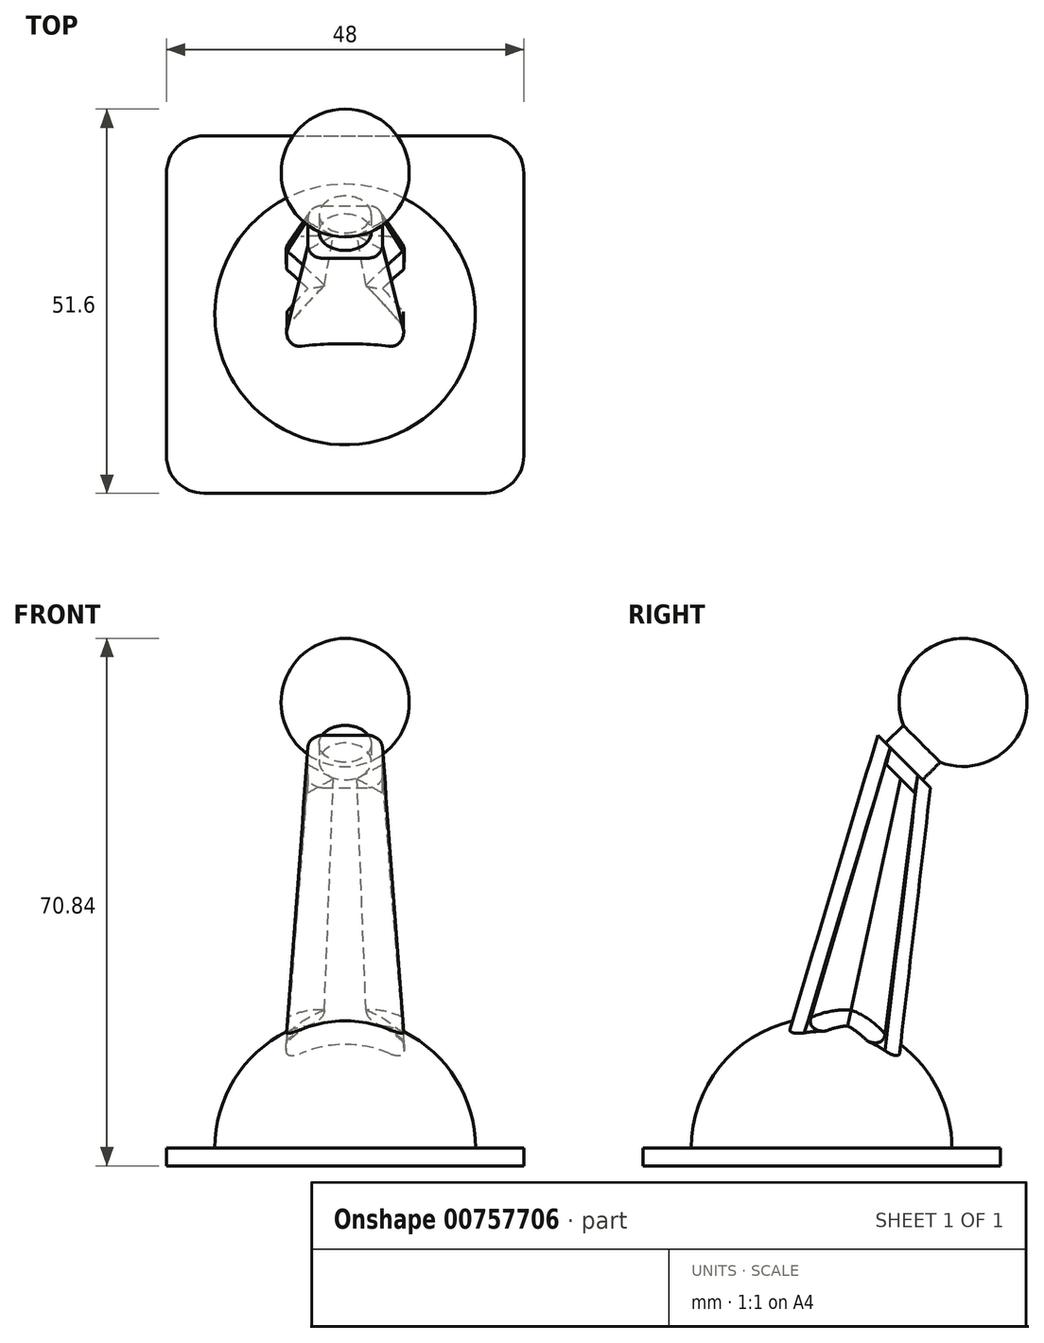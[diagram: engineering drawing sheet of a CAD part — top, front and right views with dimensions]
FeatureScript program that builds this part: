
annotation { "Feature Type Name" : "Feature", "Feature Type Description" : "" }
export const myFeature = defineFeature(function(context is Context, id is Id, definition is map)
    precondition{}
    {
        {
            var Q0;
            Q0=qCreatedBy(makeId("Top.planeOp"),FACE);
            var sketch = newSketch(context, id + "F0", { "sketchPlane" : qUnion([Q0])});
            skLineSegment(sketch, "E0.bottom", {"start": v(-24, 24) * mm, "end": v(24, 24) * mm});
            skLineSegment(sketch, "E0.top", {"start": v(-24, -24) * mm, "end": v(24, -24) * mm});
            skLineSegment(sketch, "E0.left", {"start": v(-24, 24) * mm, "end": v(-24, -24) * mm});
            skLineSegment(sketch, "E0.right", {"start": v(24, 24) * mm, "end": v(24, -24) * mm});
            skPoint(sketch, "E0.middle", {"position": v(0, 0) * mm});
            skSolve(sketch);
        }
        {
            var Q0;
            Q0 = qSketchRegion(id + "F0", true);
            extrude(context, id + "F1", {"entities" : qUnion([Q0]), "oppositeDirection" : true, "depth" : 2.4 * mm, "offsetDistance" : 25 * mm});
        }
        {
            var Q0;
            Q0=makeQuery(id+"F1.opExtrude","CAP_FACE",FACE,{"disambiguationData":[OSD([sQuery(id+"F0.wireOp",EDGE,"E0.bottom"),sQuery(id+"F0.wireOp",EDGE,"E0.top"),sQuery(id+"F0.wireOp",EDGE,"E0.left"),sQuery(id+"F0.wireOp",EDGE,"E0.right")])],"isStart":true});
            var sketch = newSketch(context, id + "F2", { "sketchPlane" : qUnion([Q0])});
            skLineSegment(sketch, "E1.bottom", {"start": v(-9, -9) * mm, "end": v(9, -9) * mm});
            skLineSegment(sketch, "E1.top", {"start": v(-9, 9) * mm, "end": v(9, 9) * mm});
            skLineSegment(sketch, "E1.left", {"start": v(-9, -9) * mm, "end": v(-9, 9) * mm});
            skLineSegment(sketch, "E1.right", {"start": v(9, -9) * mm, "end": v(9, 9) * mm});
            skPoint(sketch, "E1.middle", {"position": v(0, 0) * mm});
            skLineSegment(sketch, "E2", {"start": v(-9, 6.6) * mm, "end": v(-3.5, 0) * mm});
            skLineSegment(sketch, "E3", {"start": v(-3.5, 0) * mm, "end": v(-9, -6.6) * mm});
            skLineSegment(sketch, "E4", {"start": v(9, 6.6) * mm, "end": v(3.5, 0) * mm});
            skLineSegment(sketch, "E5", {"start": v(3.5, 0) * mm, "end": v(9, -6.6) * mm});
            skSolve(sketch);
        }
        {
            var Q0;
            {var subQ4=sQuery(id+"F2.wireOp",EDGE,"E1.bottom");Q0=makeQuery(id+"F2.imprint","IMPRINT",FACE,{"disambiguationData":[TD([[makeQuery(id+"F2.imprint","IMPRINT",EDGE,{"derivedFrom":subQ4}),-1.0]])]});}
            cPlane(context, id + "F3", {"entities" : qUnion([Q0]), "cplaneType" : CPlaneType.OFFSET, "offset" : 45 * mm, "width" : 150 * mm, "height" : 150 * mm});
        }
        {
            var Q0;
            Q0=qCreatedBy(id+"F3.planeOp",FACE);
            var sketch = newSketch(context, id + "F4", { "sketchPlane" : qUnion([Q0])});
            skLineSegment(sketch, "E6", {"start": v(11.73, 18) * mm, "end": v(-9.75, 18) * mm, "construction": true});
            skSolve(sketch);
        }
        {
            var Q0;
            Q0=sQuery(id+"F4.wireOp",EDGE,"E6");
            cPlane(context, id + "F5", {"entities" : qUnion([Q0]), "cplaneType" : CPlaneType.LINE_ANGLE, "offset" : 25 * mm, "angle" : 45 * degree, "oppositeDirection" : true, "width" : 150 * mm, "height" : 150 * mm});
        }
        {
            var Q0;
            Q0=qCreatedBy(id+"F5.planeOp",FACE);
            var sketch = newSketch(context, id + "F6", { "sketchPlane" : qUnion([Q0])});
            skLineSegment(sketch, "E7.bottom", {"start": v(-5, 23.87) * mm, "end": v(5, 23.87) * mm});
            skLineSegment(sketch, "E7.top", {"start": v(-5, 33.87) * mm, "end": v(5, 33.87) * mm});
            skLineSegment(sketch, "E7.left", {"start": v(-5, 23.87) * mm, "end": v(-5, 33.87) * mm});
            skLineSegment(sketch, "E7.right", {"start": v(5, 23.87) * mm, "end": v(5, 33.87) * mm});
            skPoint(sketch, "E7.middle", {"position": v(0, 28.87) * mm});
            skLineSegment(sketch, "E8", {"start": v(5, 31.47) * mm, "end": v(1.5, 28.87) * mm});
            skLineSegment(sketch, "E9", {"start": v(1.5, 28.87) * mm, "end": v(5, 26.27) * mm});
            skLineSegment(sketch, "E10", {"start": v(-5, 31.47) * mm, "end": v(-1.5, 28.87) * mm});
            skLineSegment(sketch, "E11", {"start": v(-1.5, 28.87) * mm, "end": v(-5, 26.35) * mm});
            skSolve(sketch);
        }
        {
            var Q1;
            {var subQ3=sQuery(id+"F2.wireOp",EDGE,"E1.bottom");Q1=makeQuery(id+"F2.imprint","IMPRINT",FACE,{"disambiguationData":[TD([[makeQuery(id+"F2.imprint","IMPRINT",EDGE,{"derivedFrom":subQ3}),1.0]])]});}
            var Q2;
            {var subQ3=sQuery(id+"F6.wireOp",EDGE,"E7.bottom");Q2=makeQuery(id+"F6.imprint","IMPRINT",FACE,{"disambiguationData":[TD([[makeQuery(id+"F6.imprint","IMPRINT",EDGE,{"derivedFrom":subQ3}),1.0]])]});}
            loft(context, id + "F7", {"operationType" : NewBodyOperationType.ADD, "sheetProfilesArray" : [{ "sheetProfileEntities" : qUnion([Q1]) }, { "sheetProfileEntities" : qUnion([Q2]) }]});
        }
        {
            var Q0;
            {var subQ0=sQuery(id+"F6.wireOp",EDGE,"E8");Q0=makeQuery(id+"F6.imprint","IMPRINT",FACE,{"disambiguationData":[TD([[makeQuery(id+"F6.imprint","IMPRINT",EDGE,{"derivedFrom":subQ0}),1.0]])]});}
            var Q1;
            {var subQ3=sQuery(id+"F6.wireOp",EDGE,"E7.bottom");Q1=makeQuery(id+"F6.imprint","IMPRINT",FACE,{"disambiguationData":[TD([[makeQuery(id+"F6.imprint","IMPRINT",EDGE,{"derivedFrom":subQ3}),1.0]])]});}
            var Q2;
            {var subQ0=sQuery(id+"F6.wireOp",EDGE,"E10");Q2=makeQuery(id+"F6.imprint","IMPRINT",FACE,{"disambiguationData":[TD([[makeQuery(id+"F6.imprint","IMPRINT",EDGE,{"derivedFrom":subQ0}),-1.0]])]});}
            extrude(context, id + "F8", {"entities" : qUnion([Q0, Q1, Q2]), "operationType" : NewBodyOperationType.ADD, "depth" : 2 * mm, "offsetDistance" : 25 * mm});
        }
        {
            var Q0;
            {var subQ3=sQuery(id+"F6.wireOp",EDGE,"E7.bottom");Q0=makeQuery(id+"F6.imprint","IMPRINT",FACE,{"disambiguationData":[TD([[makeQuery(id+"F6.imprint","IMPRINT",EDGE,{"derivedFrom":subQ3}),1.0]])]});}
            var sketch = newSketch(context, id + "F9", { "sketchPlane" : qUnion([Q0])});
            skCircle(sketch, "E12", {"center": v(0, 28.87) * mm, "radius": 3.5 * mm});
            skSolve(sketch);
        }
        {
            var Q0;
            Q0=makeQuery(id+"F9.imprint","IMPRINT",FACE,{"disambiguationData":[TD([[makeQuery(id+"F9.imprint","IMPRINT",EDGE,{"derivedFrom":sQuery(id+"F9.wireOp",EDGE,"E12")}),1.0]])]});
            var Q1;
            {var subQ0=sQuery(id+"F9.wireOp",EDGE,"E12");var subQ1=makeQuery(id+"F6.imprint","IMPRINT",EDGE,{"derivedFrom":sQuery(id+"F6.wireOp",EDGE,"E10")});var subQ2=makeQuery(id+"F9.imprint","INTERSECT",VERTEX,{"derivedFrom":[subQ1,subQ0]});Q1=makeQuery(id+"F9.imprint","IMPRINT",FACE,{"disambiguationData":[TD([[makeQuery(id+"F9.imprint","IMPRINT",EDGE,{"disambiguationData":[TD([[subQ2,-1.0]])],"derivedFrom":subQ0}),1.0]])]});}
            var Q2;
            {var subQ0=sQuery(id+"F9.wireOp",EDGE,"E12");var subQ1=makeQuery(id+"F6.imprint","IMPRINT",EDGE,{"derivedFrom":sQuery(id+"F6.wireOp",EDGE,"E8")});var subQ2=makeQuery(id+"F9.imprint","INTERSECT",VERTEX,{"derivedFrom":[subQ1,subQ0]});Q2=makeQuery(id+"F9.imprint","IMPRINT",FACE,{"disambiguationData":[TD([[makeQuery(id+"F9.imprint","IMPRINT",EDGE,{"disambiguationData":[TD([[subQ2,1.0]])],"derivedFrom":subQ0}),1.0]])]});}
            extrude(context, id + "F10", {"entities" : qUnion([Q0, Q1, Q2]), "operationType" : NewBodyOperationType.ADD, "oppositeDirection" : true, "depth" : 3.4 * mm, "offsetDistance" : 25 * mm});
        }
        {
            var Q0;
            Q0=qCreatedBy(makeId("Right.planeOp"),FACE);
            var sketch = newSketch(context, id + "F11", { "sketchPlane" : qUnion([Q0])});
            skLineSegment(sketch, "E13", {"start": v(11.06, 51.9) * mm, "end": v(-10.15, 30.68) * mm, "construction": true});
            skArc(sketch, "E14", {"start": v(12.92, 53.76) * mm, "mid": v(25.08, 53.76) * mm, "end": v(25.08, 65.92) * mm});
            skLineSegment(sketch, "E15", {"start": v(8.17, 59.63) * mm, "end": v(21.18, 46.63) * mm, "construction": true});
            skLineSegment(sketch, "E16", {"start": v(11.82, 47.7) * mm, "end": v(6.68, 42.56) * mm, "construction": true});
            skLineSegment(sketch, "E17", {"start": v(12.92, 53.76) * mm, "end": v(25.08, 65.92) * mm});
            skSolve(sketch);
        }
        {
            var Q0;
            Q0=makeQuery(id+"F11.imprint","IMPRINT",FACE,{"disambiguationData":[TD([[makeQuery(id+"F11.imprint","IMPRINT",EDGE,{"derivedFrom":sQuery(id+"F11.wireOp",EDGE,"E14")}),1.0]])]});
            var Q1;
            Q1=sQuery(id+"F11.wireOp",EDGE,"E13");
            revolve(context, id + "F12", {"operationType" : NewBodyOperationType.ADD, "surfaceOperationType" : NewSurfaceOperationType.NEW, "entities" : qUnion([Q0]), "axis" : qUnion([Q1]), "revolveType" : RevolveType.FULL});
        }
        {
            var Q0;
            Q0=qCreatedBy(makeId("Right.planeOp"),FACE);
            var sketch = newSketch(context, id + "F13", { "sketchPlane" : qUnion([Q0])});
            skArc(sketch, "E18", {"start": v(0, 17.5) * mm, "mid": v(-12.37, 12.37) * mm, "end": v(-17.5, 0) * mm});
            skLineSegment(sketch, "E19", {"start": v(-17.5, 0) * mm, "end": v(0, 0) * mm});
            skLineSegment(sketch, "E20", {"start": v(0, 0) * mm, "end": v(0, 27.64) * mm, "construction": true});
            skPoint(sketch, "E20.endSnap0", {"position": v(0, 17.5) * mm});
            skLineSegment(sketch, "E21", {"start": v(0, 17.5) * mm, "end": v(0, 0) * mm});
            skSolve(sketch);
        }
        {
            var Q0;
            Q0 = qSketchRegion(id + "F13", true);
            var Q1;
            Q1=sQuery(id+"F13.wireOp",EDGE,"E20");
            revolve(context, id + "F14", {"operationType" : NewBodyOperationType.ADD, "surfaceOperationType" : NewSurfaceOperationType.NEW, "entities" : qUnion([Q0]), "axis" : qUnion([Q1]), "revolveType" : RevolveType.FULL});
        }
        {
            var Q0;
            {var subQ1=sQuery(id+"F6.wireOp",EDGE,"E7.left");var subQ2=sQuery(id+"F6.wireOp",EDGE,"E7.top");Q0=makeQuery(id+"F8.boolean.opBoolean","SPLIT",FACE,{"disambiguationData":[TD([makeQuery(id+"F8.opExtrude","SWEPT_FACE",FACE,{"disambiguationData":[OSD([subQ2])]})])],"derivedFrom":makeQuery(id+"F8.opExtrude","SWEPT_FACE",FACE,{"disambiguationData":[OSD([subQ1])]})});}
            extrude(context, id + "F15", {"entities" : qUnion([Q0]), "operationType" : NewBodyOperationType.REMOVE, "oppositeDirection" : true, "depth" : 25 * mm, "offsetDistance" : 25 * mm});
        }
        {
            var Q0;
            Q0=makeQuery(id+"F7.opLoft","SWEPT_EDGE",EDGE,{"disambiguationData":[OSD([sQuery(id+"F2.wireOp",EDGE,"E1.top"),sQuery(id+"F2.wireOp",EDGE,"E1.left"),sQuery(id+"F6.wireOp",EDGE,"E7.bottom"),sQuery(id+"F6.wireOp",EDGE,"E7.left")])]});
            var Q1;
            Q1=makeQuery(id+"F7.opLoft","SWEPT_EDGE",EDGE,{"disambiguationData":[OSD([sQuery(id+"F2.wireOp",EDGE,"E1.bottom"),sQuery(id+"F2.wireOp",EDGE,"E1.left"),sQuery(id+"F6.wireOp",EDGE,"E7.top"),sQuery(id+"F6.wireOp",EDGE,"E7.left")])]});
            var Q2;
            Q2=makeQuery(id+"F7.opLoft","SWEPT_EDGE",EDGE,{"disambiguationData":[OSD([sQuery(id+"F2.wireOp",EDGE,"E1.bottom"),sQuery(id+"F2.wireOp",EDGE,"E1.right"),sQuery(id+"F6.wireOp",EDGE,"E7.top"),sQuery(id+"F6.wireOp",EDGE,"E7.right")])]});
            var Q3;
            Q3=makeQuery(id+"F7.opLoft","SWEPT_EDGE",EDGE,{"disambiguationData":[OSD([sQuery(id+"F2.wireOp",EDGE,"E1.top"),sQuery(id+"F2.wireOp",EDGE,"E1.right"),sQuery(id+"F6.wireOp",EDGE,"E7.bottom"),sQuery(id+"F6.wireOp",EDGE,"E7.right")])]});
            var Q4;
            {var subQ0=sQuery(id+"F6.wireOp",EDGE,"E10");var subQ1=sQuery(id+"F6.wireOp",EDGE,"E11");var subQ2=sQuery(id+"F6.wireOp",EDGE,"E7.left");var subQ3=sQuery(id+"F2.wireOp",EDGE,"E3");var subQ4=sQuery(id+"F2.wireOp",EDGE,"E1.left");var subQ5=sQuery(id+"F2.wireOp",EDGE,"E2");Q4=makeQuery(id+"F14.boolean.opBoolean","INTERSECT",EDGE,{"derivedFrom":[makeQuery(id+"F7.opLoft","SWEPT_FACE",FACE,{"disambiguationData":[OSD([subQ4,subQ5,subQ3,subQ2,subQ0,subQ1]),TDD([makeQuery(id+"F2.imprint","INTERSECT",VERTEX,{"derivedFrom":[subQ5,subQ3]}),makeQuery(id+"F2.imprint","INTERSECT",VERTEX,{"derivedFrom":[subQ4,subQ3]}),makeQuery(id+"F2.imprint","IMPRINT",EDGE,{"derivedFrom":subQ3}),makeQuery(id+"F6.imprint","INTERSECT",VERTEX,{"derivedFrom":[subQ2,subQ0]}),makeQuery(id+"F6.imprint","INTERSECT",VERTEX,{"derivedFrom":[subQ0,subQ1]}),makeQuery(id+"F6.imprint","IMPRINT",EDGE,{"derivedFrom":subQ0})])]}),makeQuery(id+"F14.opRevolve","SWEPT_FACE",FACE,{"disambiguationData":[OSD([sQuery(id+"F13.wireOp",EDGE,"E18")])]})]});}
            var Q5;
            {var subQ0=sQuery(id+"F6.wireOp",EDGE,"E11");var subQ1=sQuery(id+"F6.wireOp",EDGE,"E7.left");var subQ2=sQuery(id+"F6.wireOp",EDGE,"E10");var subQ3=sQuery(id+"F2.wireOp",EDGE,"E2");var subQ4=sQuery(id+"F2.wireOp",EDGE,"E3");var subQ5=sQuery(id+"F2.wireOp",EDGE,"E1.left");Q5=makeQuery(id+"F14.boolean.opBoolean","INTERSECT",EDGE,{"derivedFrom":[makeQuery(id+"F7.opLoft","SWEPT_FACE",FACE,{"disambiguationData":[OSD([subQ5,subQ3,subQ4,subQ1,subQ2,subQ0]),TDD([makeQuery(id+"F2.imprint","INTERSECT",VERTEX,{"derivedFrom":[subQ5,subQ3]}),makeQuery(id+"F2.imprint","INTERSECT",VERTEX,{"derivedFrom":[subQ3,subQ4]}),makeQuery(id+"F2.imprint","IMPRINT",EDGE,{"derivedFrom":subQ3}),makeQuery(id+"F6.imprint","INTERSECT",VERTEX,{"derivedFrom":[subQ2,subQ0]}),makeQuery(id+"F6.imprint","INTERSECT",VERTEX,{"derivedFrom":[subQ1,subQ0]}),makeQuery(id+"F6.imprint","IMPRINT",EDGE,{"derivedFrom":subQ0})])]}),makeQuery(id+"F14.opRevolve","SWEPT_FACE",FACE,{"disambiguationData":[OSD([sQuery(id+"F13.wireOp",EDGE,"E18")])]})]});}
            var Q6;
            {var subQ0=sQuery(id+"F6.wireOp",EDGE,"E8");var subQ1=sQuery(id+"F6.wireOp",EDGE,"E9");var subQ2=sQuery(id+"F6.wireOp",EDGE,"E7.right");var subQ3=sQuery(id+"F2.wireOp",EDGE,"E5");var subQ4=sQuery(id+"F2.wireOp",EDGE,"E1.right");var subQ5=sQuery(id+"F2.wireOp",EDGE,"E4");Q6=makeQuery(id+"F14.boolean.opBoolean","INTERSECT",EDGE,{"derivedFrom":[makeQuery(id+"F7.opLoft","SWEPT_FACE",FACE,{"disambiguationData":[OSD([subQ4,subQ5,subQ3,subQ2,subQ0,subQ1]),TDD([makeQuery(id+"F2.imprint","INTERSECT",VERTEX,{"derivedFrom":[subQ5,subQ3]}),makeQuery(id+"F2.imprint","INTERSECT",VERTEX,{"derivedFrom":[subQ4,subQ3]}),makeQuery(id+"F2.imprint","IMPRINT",EDGE,{"derivedFrom":subQ3}),makeQuery(id+"F6.imprint","INTERSECT",VERTEX,{"derivedFrom":[subQ2,subQ0]}),makeQuery(id+"F6.imprint","INTERSECT",VERTEX,{"derivedFrom":[subQ0,subQ1]}),makeQuery(id+"F6.imprint","IMPRINT",EDGE,{"derivedFrom":subQ0})])]}),makeQuery(id+"F14.opRevolve","SWEPT_FACE",FACE,{"disambiguationData":[OSD([sQuery(id+"F13.wireOp",EDGE,"E18")])]})]});}
            var Q7;
            {var subQ0=sQuery(id+"F6.wireOp",EDGE,"E9");var subQ1=sQuery(id+"F6.wireOp",EDGE,"E7.right");var subQ2=sQuery(id+"F6.wireOp",EDGE,"E8");var subQ3=sQuery(id+"F2.wireOp",EDGE,"E4");var subQ4=sQuery(id+"F2.wireOp",EDGE,"E5");var subQ5=sQuery(id+"F2.wireOp",EDGE,"E1.right");Q7=makeQuery(id+"F14.boolean.opBoolean","INTERSECT",EDGE,{"derivedFrom":[makeQuery(id+"F7.opLoft","SWEPT_FACE",FACE,{"disambiguationData":[OSD([subQ5,subQ3,subQ4,subQ1,subQ2,subQ0]),TDD([makeQuery(id+"F2.imprint","INTERSECT",VERTEX,{"derivedFrom":[subQ5,subQ3]}),makeQuery(id+"F2.imprint","INTERSECT",VERTEX,{"derivedFrom":[subQ3,subQ4]}),makeQuery(id+"F2.imprint","IMPRINT",EDGE,{"derivedFrom":subQ3}),makeQuery(id+"F6.imprint","INTERSECT",VERTEX,{"derivedFrom":[subQ2,subQ0]}),makeQuery(id+"F6.imprint","INTERSECT",VERTEX,{"derivedFrom":[subQ1,subQ0]}),makeQuery(id+"F6.imprint","IMPRINT",EDGE,{"derivedFrom":subQ0})])]}),makeQuery(id+"F14.opRevolve","SWEPT_FACE",FACE,{"disambiguationData":[OSD([sQuery(id+"F13.wireOp",EDGE,"E18")])]})]});}
            fillet(context, id + "F16", {"entities" : qUnion([Q0, Q1, Q2, Q3, Q4, Q5, Q6, Q7]), "radius" : 2 * mm, "tangentPropagation" : true, "allowEdgeOverflow" : false});
        }
        {
            var Q0;
            Q0=makeQuery(id+"F1.opExtrude","SWEPT_EDGE",EDGE,{"disambiguationData":[OSD([sQuery(id+"F0.wireOp",EDGE,"E0.bottom"),sQuery(id+"F0.wireOp",EDGE,"E0.right")])]});
            var Q1;
            Q1=makeQuery(id+"F1.opExtrude","SWEPT_EDGE",EDGE,{"disambiguationData":[OSD([sQuery(id+"F0.wireOp",EDGE,"E0.bottom"),sQuery(id+"F0.wireOp",EDGE,"E0.left")])]});
            var Q2;
            Q2=makeQuery(id+"F1.opExtrude","SWEPT_EDGE",EDGE,{"disambiguationData":[OSD([sQuery(id+"F0.wireOp",EDGE,"E0.top"),sQuery(id+"F0.wireOp",EDGE,"E0.left")])]});
            var Q3;
            Q3=makeQuery(id+"F1.opExtrude","SWEPT_EDGE",EDGE,{"disambiguationData":[OSD([sQuery(id+"F0.wireOp",EDGE,"E0.top"),sQuery(id+"F0.wireOp",EDGE,"E0.right")])]});
            fillet(context, id + "F17", {"entities" : qUnion([Q0, Q1, Q2, Q3]), "radius" : 5 * mm, "tangentPropagation" : true, "allowEdgeOverflow" : false});
        }
    });
